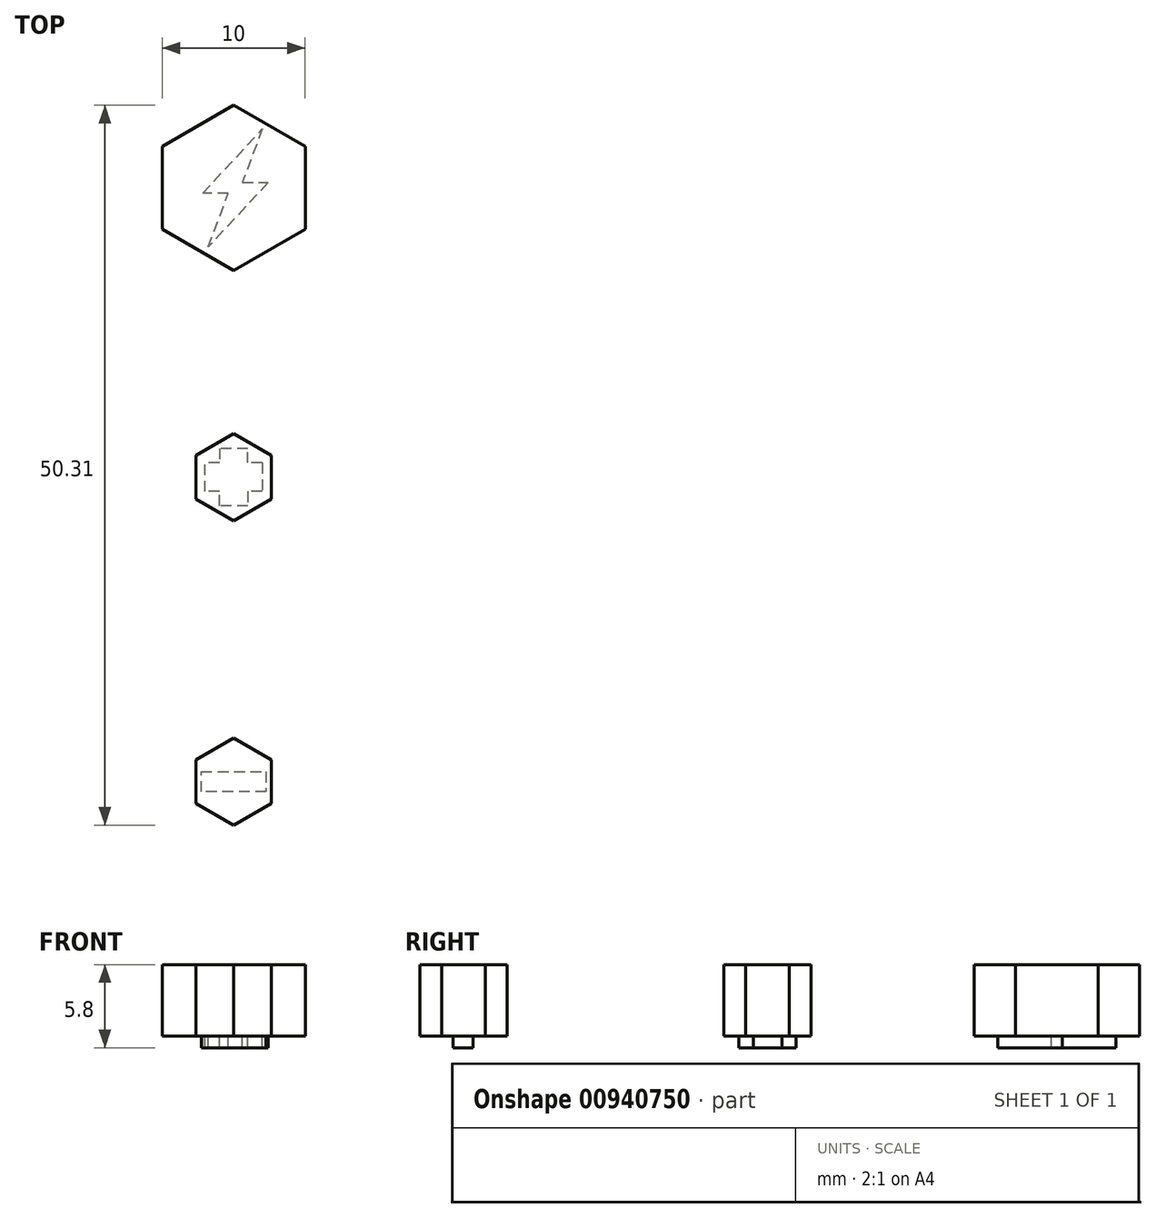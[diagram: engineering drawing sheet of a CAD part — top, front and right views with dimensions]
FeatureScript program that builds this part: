
annotation { "Feature Type Name" : "Feature", "Feature Type Description" : "" }
export const myFeature = defineFeature(function(context is Context, id is Id, definition is map)
    precondition{}
    {
        {
            var Q0;
            Q0=qCreatedBy(makeId("Top.planeOp"),FACE);
            var sketch = newSketch(context, id + "F0", { "sketchPlane" : qUnion([Q0])});
            skCircle(sketch, "E0.cCircle", {"center": v(-3.34, 17.56) * mm, "radius": 3.05 * mm, "construction": true});
            skLineSegment(sketch, "E0.0", {"start": v(-0.7, 16.04) * mm, "end": v(-3.34, 14.51) * mm});
            skLineSegment(sketch, "E0.1", {"start": v(-3.34, 14.51) * mm, "end": v(-5.98, 16.04) * mm});
            skLineSegment(sketch, "E0.2", {"start": v(-5.98, 16.04) * mm, "end": v(-5.98, 19.09) * mm});
            skLineSegment(sketch, "E0.3", {"start": v(-5.98, 19.09) * mm, "end": v(-3.34, 20.61) * mm});
            skLineSegment(sketch, "E0.4", {"start": v(-3.34, 20.61) * mm, "end": v(-0.7, 19.09) * mm});
            skLineSegment(sketch, "E0.5", {"start": v(-0.7, 19.09) * mm, "end": v(-0.7, 16.04) * mm});
            skCircle(sketch, "E1.cCircle", {"center": v(-3.34, 37.77) * mm, "radius": 5.77 * mm, "construction": true});
            skLineSegment(sketch, "E1.0", {"start": v(-3.34, 32) * mm, "end": v(-8.34, 34.89) * mm});
            skLineSegment(sketch, "E1.1", {"start": v(-8.34, 34.89) * mm, "end": v(-8.34, 40.66) * mm});
            skLineSegment(sketch, "E1.2", {"start": v(-8.34, 40.66) * mm, "end": v(-3.34, 43.55) * mm});
            skLineSegment(sketch, "E1.3", {"start": v(-3.34, 43.55) * mm, "end": v(1.66, 40.66) * mm});
            skLineSegment(sketch, "E1.4", {"start": v(1.66, 40.66) * mm, "end": v(1.66, 34.89) * mm});
            skLineSegment(sketch, "E1.5", {"start": v(1.66, 34.89) * mm, "end": v(-3.34, 32) * mm});
            skCircle(sketch, "E2.cCircle", {"center": v(-3.34, -3.7) * mm, "radius": 3.05 * mm, "construction": true});
            skLineSegment(sketch, "E2.0", {"start": v(-3.34, -6.76) * mm, "end": v(-5.98, -5.23) * mm});
            skLineSegment(sketch, "E2.1", {"start": v(-5.98, -5.23) * mm, "end": v(-5.98, -2.18) * mm});
            skLineSegment(sketch, "E2.2", {"start": v(-5.98, -2.18) * mm, "end": v(-3.34, -0.66) * mm});
            skLineSegment(sketch, "E2.3", {"start": v(-3.34, -0.66) * mm, "end": v(-0.7, -2.18) * mm});
            skLineSegment(sketch, "E2.4", {"start": v(-0.7, -2.18) * mm, "end": v(-0.7, -5.23) * mm});
            skLineSegment(sketch, "E2.5", {"start": v(-0.7, -5.23) * mm, "end": v(-3.34, -6.76) * mm});
            skCircle(sketch, "E3", {"center": v(-3.34, 37.77) * mm, "radius": 9 * mm});
            skCircle(sketch, "E4", {"center": v(-3.34, 17.56) * mm, "radius": 5.55 * mm});
            skCircle(sketch, "E5", {"center": v(-3.34, -3.73) * mm, "radius": 5.55 * mm});
            skSolve(sketch);
        }
        {
            var Q0;
            Q0=qCreatedBy(makeId("Top.planeOp"),FACE);
            var sketch = newSketch(context, id + "F1", { "sketchPlane" : qUnion([Q0])});
            skLineSegment(sketch, "E6", {"start": v(-2.73, 38.15) * mm, "end": v(-0.93, 38.15) * mm});
            skLineSegment(sketch, "E7", {"start": v(-0.93, 38.15) * mm, "end": v(-5.1, 33.65) * mm});
            skLineSegment(sketch, "E8", {"start": v(-5.1, 33.65) * mm, "end": v(-3.71, 37.4) * mm});
            skLineSegment(sketch, "E9", {"start": v(-3.71, 37.4) * mm, "end": v(-5.51, 37.4) * mm});
            skLineSegment(sketch, "E10", {"start": v(-5.51, 37.4) * mm, "end": v(-1.33, 41.9) * mm});
            skLineSegment(sketch, "E11", {"start": v(-1.33, 41.9) * mm, "end": v(-2.73, 38.15) * mm});
            skLineSegment(sketch, "E12", {"start": v(-5.34, 17.56) * mm, "end": v(-1.34, 17.56) * mm});
            skLineSegment(sketch, "E13", {"start": v(-1.34, 17.56) * mm, "end": v(-1.34, 18.56) * mm});
            skLineSegment(sketch, "E14", {"start": v(-1.34, 18.56) * mm, "end": v(-2.34, 18.56) * mm});
            skLineSegment(sketch, "E15", {"start": v(-2.34, 18.56) * mm, "end": v(-2.34, 19.56) * mm});
            skLineSegment(sketch, "E16", {"start": v(-2.34, 19.56) * mm, "end": v(-4.34, 19.56) * mm});
            skLineSegment(sketch, "E17", {"start": v(-4.34, 19.56) * mm, "end": v(-4.34, 18.56) * mm});
            skLineSegment(sketch, "E18", {"start": v(-4.34, 18.56) * mm, "end": v(-5.34, 18.56) * mm});
            skLineSegment(sketch, "E19", {"start": v(-5.34, 18.56) * mm, "end": v(-5.34, 17.56) * mm});
            skLineSegment(sketch, "E20.MirrorCS", {"start": v(-5.34, 16.56) * mm, "end": v(-5.34, 17.56) * mm});
            skLineSegment(sketch, "E21.MirrorCS", {"start": v(-4.34, 16.56) * mm, "end": v(-5.34, 16.56) * mm});
            skLineSegment(sketch, "E22.MirrorCS", {"start": v(-4.34, 15.56) * mm, "end": v(-4.34, 16.56) * mm});
            skLineSegment(sketch, "E23.MirrorCS", {"start": v(-2.34, 15.56) * mm, "end": v(-4.34, 15.56) * mm});
            skLineSegment(sketch, "E24.MirrorCS", {"start": v(-2.34, 16.56) * mm, "end": v(-2.34, 15.56) * mm});
            skLineSegment(sketch, "E25.MirrorCS", {"start": v(-1.34, 16.56) * mm, "end": v(-2.34, 16.56) * mm});
            skLineSegment(sketch, "E26.MirrorCS", {"start": v(-1.34, 17.56) * mm, "end": v(-1.34, 16.56) * mm});
            skLineSegment(sketch, "E27", {"start": v(-5.6, -3.03) * mm, "end": v(-1.07, -3.03) * mm});
            skLineSegment(sketch, "E28", {"start": v(-1.07, -3.03) * mm, "end": v(-1.07, -4.43) * mm});
            skLineSegment(sketch, "E29", {"start": v(-1.07, -4.43) * mm, "end": v(-5.6, -4.43) * mm});
            skLineSegment(sketch, "E30", {"start": v(-5.6, -4.43) * mm, "end": v(-5.6, -3.03) * mm});
            skLineSegment(sketch, "E31", {"start": v(-3.34, -3.03) * mm, "end": v(-3.34, -4.43) * mm});
            skSolve(sketch);
        }
        {
            var Q0;
            Q0=makeQuery(id+"F0.imprint","IMPRINT",FACE,{"disambiguationData":[TD([[makeQuery(id+"F0.imprint","IMPRINT",EDGE,{"derivedFrom":sQuery(id+"F0.wireOp",EDGE,"E0.0")}),-1.0]])]});
            var Q1;
            Q1=makeQuery(id+"F0.imprint","IMPRINT",FACE,{"disambiguationData":[TD([[makeQuery(id+"F0.imprint","IMPRINT",EDGE,{"derivedFrom":sQuery(id+"F0.wireOp",EDGE,"E2.0")}),-1.0]])]});
            var Q2;
            Q2=makeQuery(id+"F0.imprint","IMPRINT",FACE,{"disambiguationData":[TD([[makeQuery(id+"F0.imprint","IMPRINT",EDGE,{"derivedFrom":sQuery(id+"F0.wireOp",EDGE,"E1.0")}),-1.0]])]});
            extrude(context, id + "F2", {"entities" : qUnion([Q0, Q1, Q2]), "depth" : 5 * mm, "offsetDistance" : 25 * mm});
        }
        {
            var Q0;
            Q0=makeQuery(id+"F1.imprint","IMPRINT",FACE,{"disambiguationData":[TD([[makeQuery(id+"F1.imprint","IMPRINT",EDGE,{"derivedFrom":sQuery(id+"F1.wireOp",EDGE,"E6")}),-1.0]])]});
            var Q1;
            Q1=makeQuery(id+"F1.imprint","IMPRINT",FACE,{"disambiguationData":[TD([[makeQuery(id+"F1.imprint","IMPRINT",EDGE,{"derivedFrom":sQuery(id+"F1.wireOp",EDGE,"E12")}),-1.0]])]});
            var Q2;
            {var subQ0=sQuery(id+"F1.wireOp",EDGE,"E28");Q2=makeQuery(id+"F1.imprint","IMPRINT",FACE,{"disambiguationData":[TD([[makeQuery(id+"F1.imprint","IMPRINT",EDGE,{"derivedFrom":subQ0}),-1.0]])]});}
            var Q3;
            {var subQ0=sQuery(id+"F1.wireOp",EDGE,"E30");Q3=makeQuery(id+"F1.imprint","IMPRINT",FACE,{"disambiguationData":[TD([[makeQuery(id+"F1.imprint","IMPRINT",EDGE,{"derivedFrom":subQ0}),-1.0]])]});}
            var Q4;
            Q4=makeQuery(id+"F1.imprint","IMPRINT",FACE,{"disambiguationData":[TD([[makeQuery(id+"F1.imprint","IMPRINT",EDGE,{"derivedFrom":sQuery(id+"F1.wireOp",EDGE,"E12")}),1.0]])]});
            extrude(context, id + "F3", {"entities" : qUnion([Q0, Q1, Q2, Q3, Q4]), "oppositeDirection" : true, "depth" : 0.8 * mm, "offsetDistance" : 25 * mm});
        }
    });
